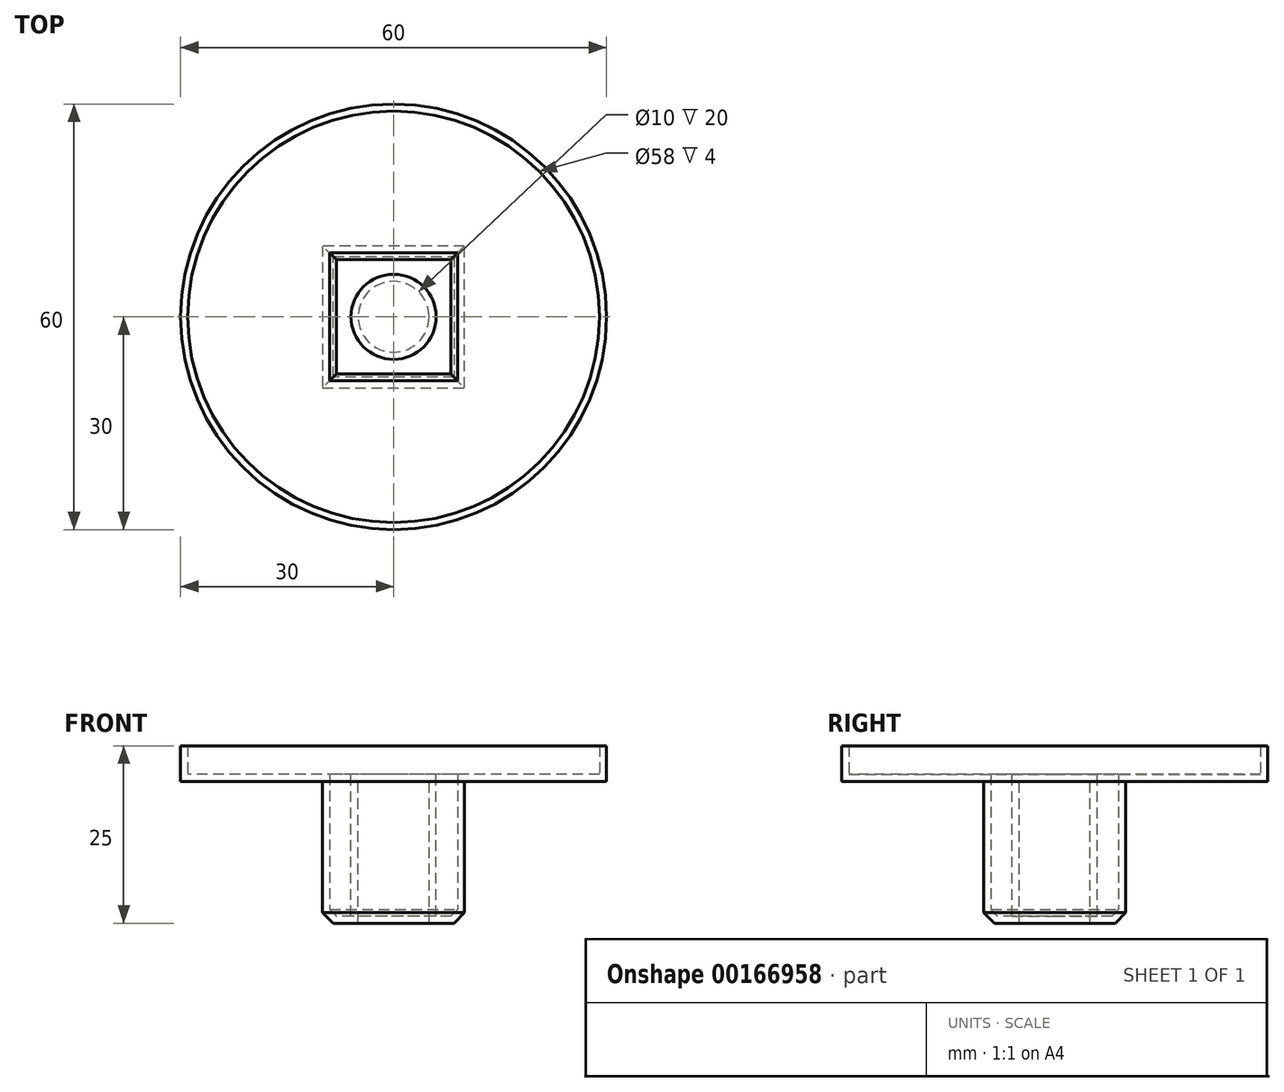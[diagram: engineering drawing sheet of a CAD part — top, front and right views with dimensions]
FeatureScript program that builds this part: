
annotation { "Feature Type Name" : "Feature", "Feature Type Description" : "" }
export const myFeature = defineFeature(function(context is Context, id is Id, definition is map)
    precondition{}
    {
        {
            var Q0;
            Q0=qCreatedBy(makeId("Top.planeOp"),FACE);
            var sketch = newSketch(context, id + "F0", { "sketchPlane" : qUnion([Q0])});
            skLineSegment(sketch, "E0.bottom", {"start": v(10, 10) * mm, "end": v(-10, 10) * mm});
            skLineSegment(sketch, "E0.top", {"start": v(10, -10) * mm, "end": v(-10, -10) * mm});
            skLineSegment(sketch, "E0.left", {"start": v(10, 10) * mm, "end": v(10, -10) * mm});
            skLineSegment(sketch, "E0.right", {"start": v(-10, 10) * mm, "end": v(-10, -10) * mm});
            skPoint(sketch, "E0.middle", {"position": v(0, 0) * mm});
            skSolve(sketch);
        }
        {
            var Q0;
            Q0 = qSketchRegion(id + "F0", true);
            extrude(context, id + "F1", {"entities" : qUnion([Q0]), "depth" : 20 * mm});
        }
        {
            var Q0;
            Q0=makeQuery(id+"F1.opExtrude","CAP_FACE",FACE,{"disambiguationData":[OSD([sQuery(id+"F0.wireOp",EDGE,"E0.bottom"),sQuery(id+"F0.wireOp",EDGE,"E0.top"),sQuery(id+"F0.wireOp",EDGE,"E0.left"),sQuery(id+"F0.wireOp",EDGE,"E0.right")])],"isStart":false});
            var sketch = newSketch(context, id + "F2", { "sketchPlane" : qUnion([Q0])});
            skCircle(sketch, "E1", {"center": v(0, 0) * mm, "radius": 5 * mm});
            skSolve(sketch);
        }
        {
            var Q0;
            Q0 = qSketchRegion(id + "F2", true);
            extrude(context, id + "F3", {"entities" : qUnion([Q0]), "operationType" : NewBodyOperationType.REMOVE, "oppositeDirection" : true, "depth" : 25 * mm});
        }
        {
            var Q0;
            Q0=makeQuery(id+"F1.opExtrude","CAP_FACE",FACE,{"disambiguationData":[OSD([sQuery(id+"F0.wireOp",EDGE,"E0.bottom"),sQuery(id+"F0.wireOp",EDGE,"E0.top"),sQuery(id+"F0.wireOp",EDGE,"E0.left"),sQuery(id+"F0.wireOp",EDGE,"E0.right")])],"isStart":false});
            var sketch = newSketch(context, id + "F4", { "sketchPlane" : qUnion([Q0])});
            skCircle(sketch, "E2", {"center": v(0, 0) * mm, "radius": 30 * mm});
            skSolve(sketch);
        }
        {
            var Q0;
            Q0 = qSketchRegion(id + "F4", true);
            extrude(context, id + "F5", {"entities" : qUnion([Q0]), "operationType" : NewBodyOperationType.ADD, "depth" : 5 * mm});
        }
        {
            var Q0;
            Q0=makeQuery(id+"F1.opExtrude","CAP_EDGE",EDGE,{"disambiguationData":[OSD([sQuery(id+"F0.wireOp",EDGE,"E0.left")])],"isStart":true});
            var Q1;
            Q1=makeQuery(id+"F1.opExtrude","CAP_EDGE",EDGE,{"disambiguationData":[OSD([sQuery(id+"F0.wireOp",EDGE,"E0.bottom")])],"isStart":true});
            var Q2;
            Q2=makeQuery(id+"F1.opExtrude","CAP_EDGE",EDGE,{"disambiguationData":[OSD([sQuery(id+"F0.wireOp",EDGE,"E0.right")])],"isStart":true});
            var Q3;
            Q3=makeQuery(id+"F1.opExtrude","CAP_EDGE",EDGE,{"disambiguationData":[OSD([sQuery(id+"F0.wireOp",EDGE,"E0.top")])],"isStart":true});
            chamfer(context, id + "F6", {"entities" : qUnion([Q0, Q1, Q2, Q3]), "width" : 1.5 * mm, "tangentPropagation" : true});
        }
        {
            var Q0;
            Q0=makeQuery(id+"F5.opExtrude","CAP_FACE",FACE,{"disambiguationData":[OSD([sQuery(id+"F4.wireOp",EDGE,"E2")])],"isStart":false});
            shell(context, id + "F7", {"entities" : qUnion([Q0]), "thickness" : 1 * mm});
        }
    });
